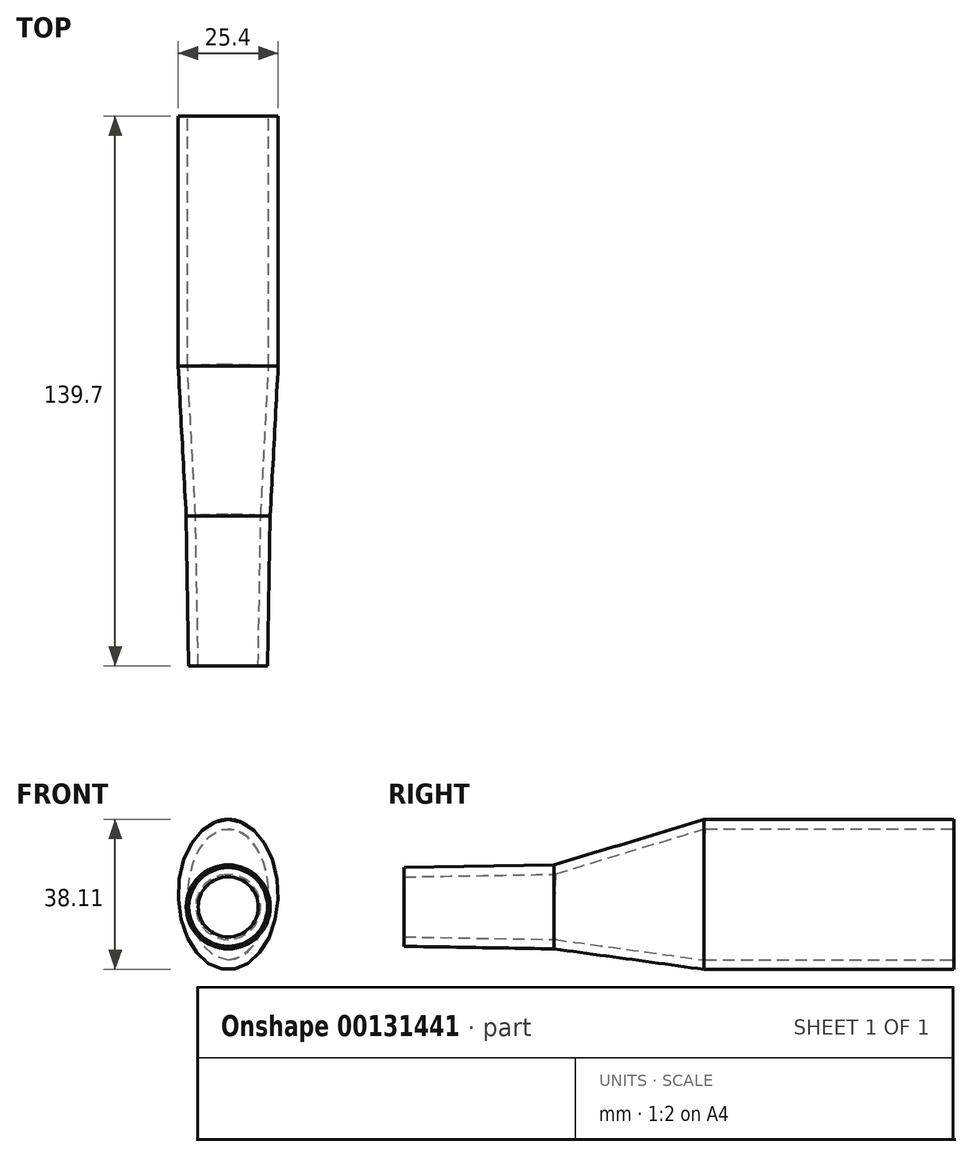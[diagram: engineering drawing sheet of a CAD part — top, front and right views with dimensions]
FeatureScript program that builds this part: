
annotation { "Feature Type Name" : "Feature", "Feature Type Description" : "" }
export const myFeature = defineFeature(function(context is Context, id is Id, definition is map)
    precondition{}
    {
        {
            var Q0;
            Q0=qCreatedBy(makeId("Front.planeOp"),FACE);
            var sketch = newSketch(context, id + "F0", { "sketchPlane" : qUnion([Q0])});
            skCircle(sketch, "E0", {"center": v(0, 0) * mm, "radius": 10 * mm});
            skSolve(sketch);
        }
        {
            var Q0;
            Q0 = qSketchRegion(id + "F0", true);
            extrude(context, id + "F1", {"entities" : qUnion([Q0]), "oppositeDirection" : true, "depth" : 38.1 * mm, "hasDraft" : true, "draftAngle" : 1 * degree});
        }
        {
            var Q0;
            Q0=qCreatedBy(makeId("Front.planeOp"),FACE);
            cPlane(context, id + "F2", {"entities" : qUnion([Q0]), "cplaneType" : CPlaneType.OFFSET, "offset" : 139.7 * mm, "oppositeDirection" : true, "width" : 152.4 * mm, "height" : 152.4 * mm});
        }
        {
            var Q0;
            Q0=qCreatedBy(id+"F2.planeOp",FACE);
            var sketch = newSketch(context, id + "F3", { "sketchPlane" : qUnion([Q0])});
            skEllipse(sketch, "E1", {"center": v(0, 3.18) * mm, "majorRadius": 19.05 * mm, "minorRadius": 12.7 * mm, "majorAxis": v(0, 1)});
            skSolve(sketch);
        }
        {
            var Q0;
            Q0=makeQuery(id+"F3.imprint","IMPRINT",FACE,{"disambiguationData":[TD([[makeQuery(id+"F3.imprint","IMPRINT",EDGE,{"derivedFrom":sQuery(id+"F3.wireOp",EDGE,"E1")}),1.0]])]});
            extrude(context, id + "F4", {"entities" : qUnion([Q0]), "depth" : 63.5 * mm});
        }
        {
            var Q1;
            Q1=makeQuery(id+"F4.opExtrude","CAP_FACE",FACE,{"disambiguationData":[OSD([sQuery(id+"F3.wireOp",EDGE,"E1")])],"isStart":false});
            var Q2;
            Q2=makeQuery(id+"F1.opExtrude","CAP_FACE",FACE,{"disambiguationData":[OSD([sQuery(id+"F0.wireOp",EDGE,"E0")])],"isStart":false});
            loft(context, id + "F5", {"operationType" : NewBodyOperationType.ADD, "sheetProfilesArray" : [{ "sheetProfileEntities" : qUnion([Q1]) }, { "sheetProfileEntities" : qUnion([Q2]) }]});
        }
        {
            var Q0;
            Q0=makeQuery(id+"F1.opExtrude","CAP_FACE",FACE,{"disambiguationData":[OSD([sQuery(id+"F0.wireOp",EDGE,"E0")])],"isStart":true});
            var Q1;
            Q1=makeQuery(id+"F4.opExtrude","CAP_FACE",FACE,{"disambiguationData":[OSD([sQuery(id+"F3.wireOp",EDGE,"E1")])],"isStart":true});
            shell(context, id + "F6", {"entities" : qUnion([Q0, Q1]), "thickness" : 2.38 * mm});
        }
    });
